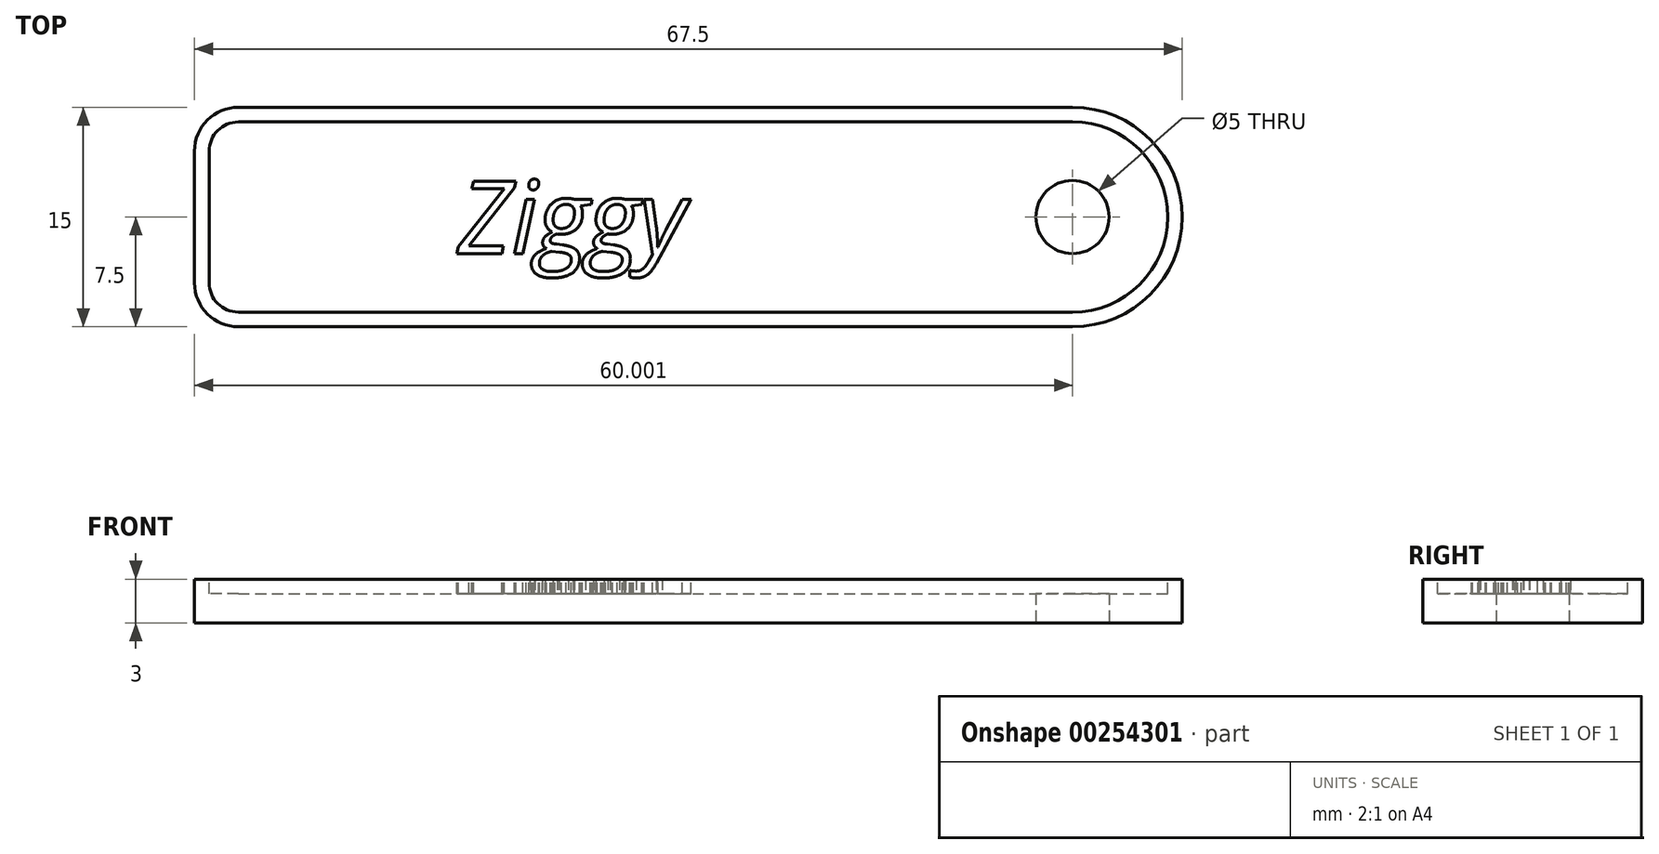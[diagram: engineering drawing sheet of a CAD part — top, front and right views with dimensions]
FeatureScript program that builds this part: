
annotation { "Feature Type Name" : "Feature", "Feature Type Description" : "" }
export const myFeature = defineFeature(function(context is Context, id is Id, definition is map)
    precondition{}
    {
        {
            var Q0;
            Q0=qCreatedBy(makeId("Top.planeOp"),FACE);
            var sketch = newSketch(context, id + "F0", { "sketchPlane" : qUnion([Q0])});
            skLineSegment(sketch, "E0.bottom", {"start": v(-12.87, 7.5) * mm, "end": v(44.13, 7.5) * mm});
            skLineSegment(sketch, "E0.top", {"start": v(-12.87, -7.5) * mm, "end": v(44.13, -7.5) * mm});
            skLineSegment(sketch, "E0.left", {"start": v(-15.87, 4.5) * mm, "end": v(-15.87, -4.5) * mm});
            skPoint(sketch, "E1.visualSharp", {"position": v(-15.87, 7.5) * mm});
            skArc(sketch, "E1.filletArc", {"start": v(-12.87, 7.5) * mm, "mid": v(-15, 6.62) * mm, "end": v(-15.87, 4.5) * mm});
            skPoint(sketch, "E2.visualSharp", {"position": v(-15.87, -7.5) * mm});
            skArc(sketch, "E2.filletArc", {"start": v(-15.87, -4.5) * mm, "mid": v(-15, -6.62) * mm, "end": v(-12.87, -7.5) * mm});
            skArc(sketch, "E3", {"start": v(44.13, -7.5) * mm, "mid": v(51.63, 0) * mm, "end": v(44.13, 7.5) * mm});
            skCircle(sketch, "E4", {"center": v(44.13, 0) * mm, "radius": 2.5 * mm});
            skSolve(sketch);
        }
        {
            var Q0;
            Q0=makeQuery(id+"F0.imprint","IMPRINT",FACE,{"disambiguationData":[TD([[makeQuery(id+"F0.imprint","IMPRINT",EDGE,{"derivedFrom":sQuery(id+"F0.wireOp",EDGE,"E0.bottom")}),-1.0]])]});
            extrude(context, id + "F1", {"entities" : qUnion([Q0]), "depth" : 3 * mm});
        }
        {
            var Q0;
            Q0=makeQuery(id+"F1.opExtrude","CAP_FACE",FACE,{"disambiguationData":[OSD([sQuery(id+"F0.wireOp",EDGE,"E0.bottom"),sQuery(id+"F0.wireOp",EDGE,"E0.top"),sQuery(id+"F0.wireOp",EDGE,"E0.left"),sQuery(id+"F0.wireOp",EDGE,"E1.filletArc"),sQuery(id+"F0.wireOp",EDGE,"E2.filletArc"),sQuery(id+"F0.wireOp",EDGE,"E3"),sQuery(id+"F0.wireOp",EDGE,"E4")])],"isStart":false});
            var sketch = newSketch(context, id + "F2", { "sketchPlane" : qUnion([Q0])});
            skText(sketch, "E5", { "text": "Ziggy", "fontName": "OpenSans-Italic.ttf"});
            skArc(sketch, "E6.0", {"start": v(-12.87, 6.5) * mm, "mid": v(-14.28, 5.91) * mm, "end": v(-14.87, 4.5) * mm});
            skArc(sketch, "E6.1", {"start": v(44.13, -6.5) * mm, "mid": v(50.63, 0) * mm, "end": v(44.13, 6.5) * mm});
            skLineSegment(sketch, "E6.2", {"start": v(-12.87, -6.5) * mm, "end": v(44.13, -6.5) * mm});
            skLineSegment(sketch, "E6.3", {"start": v(-12.87, 6.5) * mm, "end": v(44.13, 6.5) * mm});
            skArc(sketch, "E6.4", {"start": v(-14.87, -4.5) * mm, "mid": v(-14.28, -5.91) * mm, "end": v(-12.87, -6.5) * mm});
            skLineSegment(sketch, "E6.5", {"start": v(-14.87, 4.5) * mm, "end": v(-14.87, -4.5) * mm});
            const initialGuessF2  = {"E5": [0.00213, -0.0025, 1, 0, 0.005]};
            skSetInitialGuess(sketch, initialGuessF2);
            skSolve(sketch);
        }
        {
            var Q0;
            Q0 = qSketchRegion(id + "F2", true);
            var Q1;
            Q1=makeQuery(id+"F2.imprint","IMPRINT",FACE,{"disambiguationData":[TD([[makeQuery(id+"F2.imprint","IMPRINT",EDGE,{"derivedFrom":sQuery(id+"F2.wireOp",EDGE,"E5.sketch_text.stroke-57")}),1.0]])]});
            var Q2;
            Q2=makeQuery(id+"F2.imprint","IMPRINT",FACE,{"disambiguationData":[TD([[makeQuery(id+"F2.imprint","IMPRINT",EDGE,{"derivedFrom":sQuery(id+"F2.wireOp",EDGE,"E5.sketch_text.stroke-48")}),1.0]])]});
            var Q3;
            Q3=makeQuery(id+"F2.imprint","IMPRINT",FACE,{"disambiguationData":[TD([[makeQuery(id+"F2.imprint","IMPRINT",EDGE,{"derivedFrom":sQuery(id+"F2.wireOp",EDGE,"E5.sketch_text.stroke-94")}),1.0]])]});
            var Q4;
            Q4=makeQuery(id+"F2.imprint","IMPRINT",FACE,{"disambiguationData":[TD([[makeQuery(id+"F2.imprint","IMPRINT",EDGE,{"derivedFrom":sQuery(id+"F2.wireOp",EDGE,"E5.sketch_text.stroke-103")}),1.0]])]});
            extrude(context, id + "F3", {"entities" : qUnion([Q0, Q1, Q2, Q3, Q4]), "operationType" : NewBodyOperationType.REMOVE, "oppositeDirection" : true, "depth" : 1 * mm});
        }
    });
